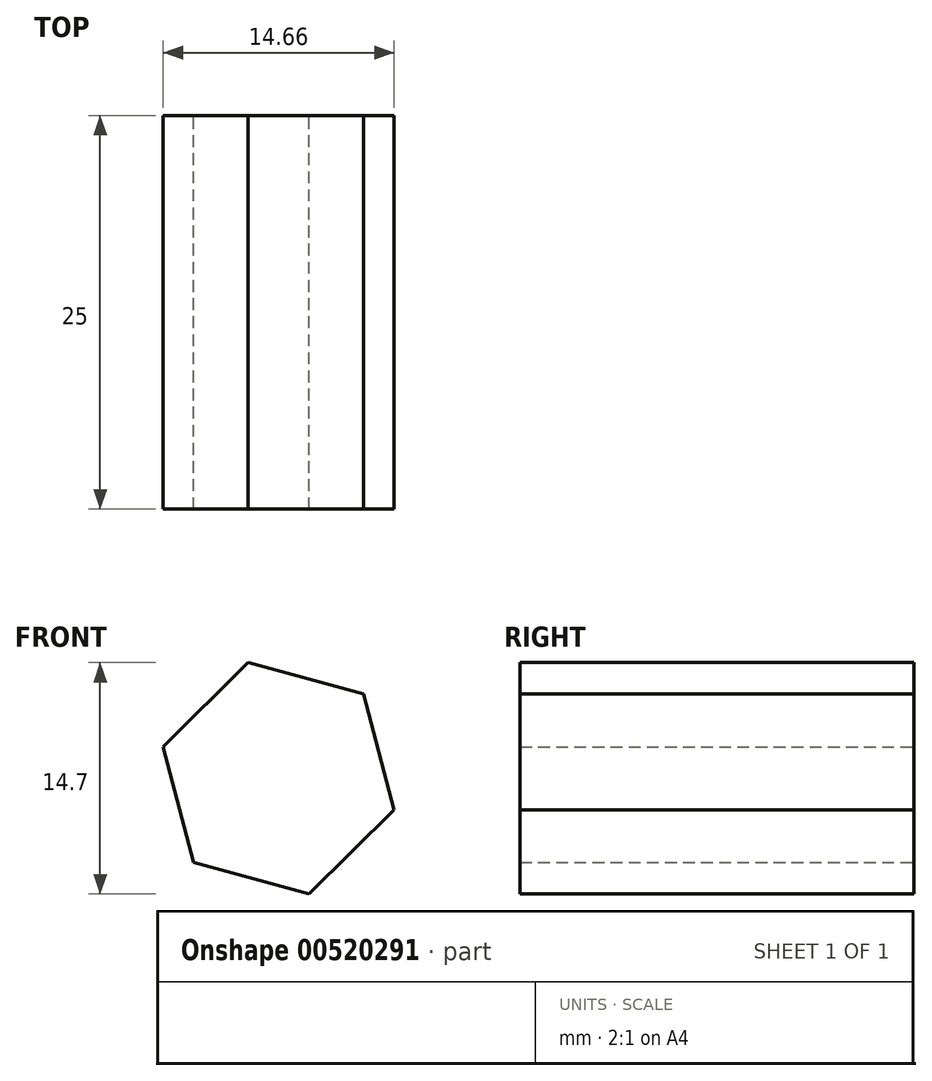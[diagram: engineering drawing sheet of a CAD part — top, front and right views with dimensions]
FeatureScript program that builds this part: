
annotation { "Feature Type Name" : "Feature", "Feature Type Description" : "" }
export const myFeature = defineFeature(function(context is Context, id is Id, definition is map)
    precondition{}
    {
        {
            var Q0;
            Q0=qCreatedBy(makeId("Front.planeOp"),FACE);
            var sketch = newSketch(context, id + "F0", { "sketchPlane" : qUnion([Q0])});
            skCircle(sketch, "E0.cCircle", {"center": v(0, 0) * mm, "radius": 6.58 * mm, "construction": true});
            skLineSegment(sketch, "E0.0", {"start": v(-5.4, -5.35) * mm, "end": v(-7.33, 2) * mm});
            skLineSegment(sketch, "E0.1", {"start": v(-7.33, 2) * mm, "end": v(-1.93, 7.35) * mm});
            skLineSegment(sketch, "E0.2", {"start": v(-1.93, 7.35) * mm, "end": v(5.4, 5.35) * mm});
            skLineSegment(sketch, "E0.3", {"start": v(5.4, 5.35) * mm, "end": v(7.33, -2) * mm});
            skLineSegment(sketch, "E0.4", {"start": v(7.33, -2) * mm, "end": v(1.93, -7.35) * mm});
            skLineSegment(sketch, "E0.5", {"start": v(1.93, -7.35) * mm, "end": v(-5.4, -5.35) * mm});
            skPoint(sketch, "E0.0.midPoint", {"position": v(-6.36, -1.68) * mm});
            skSolve(sketch);
        }
        {
            var Q0;
            Q0 = qSketchRegion(id + "F0", true);
            extrude(context, id + "F1", {"entities" : qUnion([Q0]), "depth" : 25 * mm, "offsetDistance" : 25 * mm});
        }
    });
